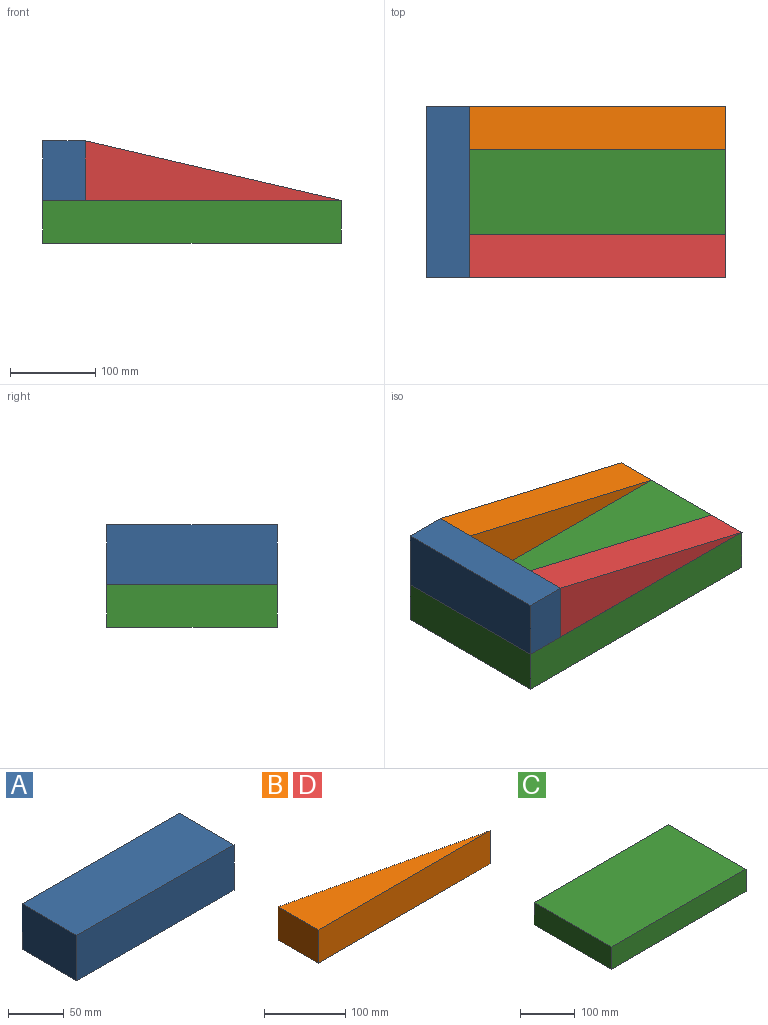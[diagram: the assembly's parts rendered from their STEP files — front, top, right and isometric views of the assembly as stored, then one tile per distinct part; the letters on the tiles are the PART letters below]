
ASSEMBLY  parts=4 mates=10
PART A: 6 faces, bbox 200x70x50 mm
  f0: plane 70x50mm, normal (-1,0,0), area 3500mm2, adj f1,f3,f4,f5
  f1: plane 200x50mm, normal (0,-1,0), area 10000mm2, adj f0,f2,f4,f5
  f2: plane 70x50mm, normal (1,0,0), area 3500mm2, adj f1,f3,f4,f5
  f3: plane 200x50mm, normal (0,1,0), area 10000mm2, adj f0,f2,f4,f5
  f4: plane 200x70mm, normal (0,0,1), area 14000mm2, adj f0,f1,f2,f3
  f5: plane 200x70mm, normal (0,0,-1), area 14000mm2, adj f0,f1,f2,f3
PART B: 5 faces, bbox 300x70x50 mm
  f0: plane 70x50mm, normal (-1,0,0), area 3500mm2, adj f1,f2,f3,f4
  f1: plane 300x50mm, normal (0,-1,0), area 15000mm2, adj f0,f2,f3,f4
  f2: plane 300x70mm, normal (0.23,0.97,0), area 15402.9mm2, adj f0,f1,f3,f4
  f3: plane 300x70mm, normal (0,0,1), area 10500mm2, adj f0,f1,f2
  f4: plane 300x70mm, normal (0,0,-1), area 10500mm2, adj f0,f1,f2
PART C: 6 faces, bbox 350x200x50 mm
  f0: plane 350x50mm, normal (0,-1,0), area 17500mm2, adj f1,f3,f4,f5
  f1: plane 200x50mm, normal (1,0,0), area 10000mm2, adj f0,f2,f4,f5
  f2: plane 350x50mm, normal (0,1,0), area 17500mm2, adj f1,f3,f4,f5
  f3: plane 200x50mm, normal (-1,0,0), area 10000mm2, adj f0,f2,f4,f5
  f4: plane 350x200mm, normal (0,0,1), area 70000mm2, adj f0,f1,f2,f3
  f5: plane 350x200mm, normal (0,0,-1), area 70000mm2, adj f0,f1,f2,f3
PART D: same geometry as B
PLACE A rot(axis=(0.58,-0.58,-0.58),120deg) t=(132.9,544.01,199.75)mm
PLACE B rot(axis=(1,0,0),90deg) t=(200.46,641.62,188.57)mm
PLACE C t=(274.06,659.95,104.83)mm
PLACE D rot(axis=(1,0,0),90deg) t=(200.46,491.62,188.57)mm
MATE planar D.f1 <-> C.f4  axis (0,0,-1) through (282.9,466.62,154.83)mm
MATE parallel A.f3 <-> C.f4  axis (0,0,1) through (132.9,441.62,224.83)mm
MATE planar A.f0 <-> C.f2  axis (0,1,0) through (107.9,641.62,189.83)mm
MATE planar A.f5 <-> B.f0  axis (1,0,0) through (132.9,541.62,189.83)mm
MATE planar D.f3 <-> C.f0  axis (0,-1,0) through (232.9,441.62,178.17)mm
MATE planar B.f1 <-> C.f4  axis (0,0,-1) through (282.9,616.62,154.83)mm
MATE planar C.f4 <-> A.f1  axis (0,0,1) through (257.9,541.62,154.83)mm
MATE planar B.f4 <-> C.f2  axis (0,1,0) through (232.9,641.62,178.17)mm
MATE planar A.f5 <-> D.f0  axis (1,0,0) through (132.9,541.62,189.83)mm
MATE planar A.f4 <-> C.f3  axis (-1,0,0) through (82.9,541.62,189.83)mm
